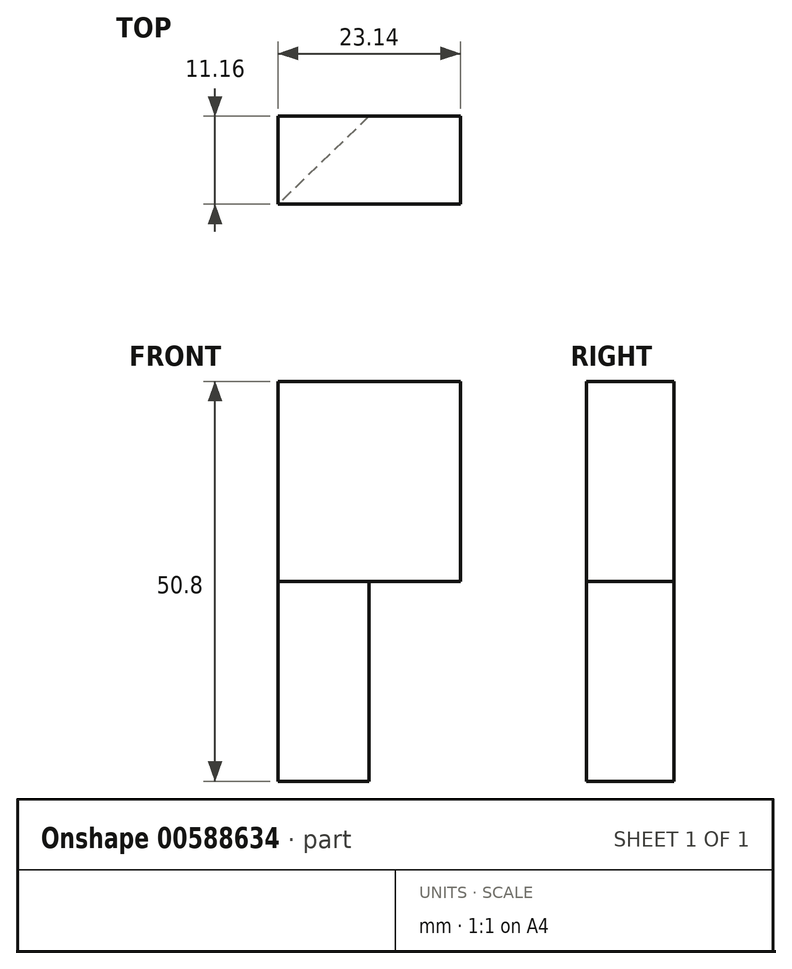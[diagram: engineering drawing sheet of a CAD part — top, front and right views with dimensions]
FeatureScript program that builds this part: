
annotation { "Feature Type Name" : "Feature", "Feature Type Description" : "" }
export const myFeature = defineFeature(function(context is Context, id is Id, definition is map)
    precondition{}
    {
        {
            var Q0;
            Q0=qCreatedBy(makeId("Top.planeOp"),FACE);
            var sketch = newSketch(context, id + "F0", { "sketchPlane" : qUnion([Q0])});
            skLineSegment(sketch, "E0.bottom", {"start": v(-11.57, -5.58) * mm, "end": v(11.57, -5.58) * mm});
            skLineSegment(sketch, "E0.top", {"start": v(-11.57, 5.58) * mm, "end": v(11.57, 5.58) * mm});
            skLineSegment(sketch, "E0.left", {"start": v(-11.57, -5.58) * mm, "end": v(-11.57, 5.58) * mm});
            skLineSegment(sketch, "E0.right", {"start": v(11.57, -5.58) * mm, "end": v(11.57, 5.58) * mm});
            skPoint(sketch, "E0.middle", {"position": v(0, 0) * mm});
            skSolve(sketch);
        }
        {
            var Q0;
            Q0=makeQuery(id+"F0.imprint","IMPRINT",FACE,{"disambiguationData":[TD([[makeQuery(id+"F0.imprint","IMPRINT",EDGE,{"derivedFrom":sQuery(id+"F0.wireOp",EDGE,"E0.bottom")}),1.0]])]});
            extrude(context, id + "F1", {"entities" : qUnion([Q0]), "depth" : 25.4 * mm, "offsetDistance" : 25.4 * mm});
        }
        {
            var Q0;
            Q0=makeQuery(id+"F1.opExtrude","CAP_FACE",FACE,{"disambiguationData":[OSD([sQuery(id+"F0.wireOp",EDGE,"E0.bottom"),sQuery(id+"F0.wireOp",EDGE,"E0.top"),sQuery(id+"F0.wireOp",EDGE,"E0.left"),sQuery(id+"F0.wireOp",EDGE,"E0.right")])],"isStart":false});
            var sketch = newSketch(context, id + "F2", { "sketchPlane" : qUnion([Q0])});
            skLineSegment(sketch, "E1", {"start": v(0, 5.58) * mm, "end": v(-11.57, -5.58) * mm});
            skSolve(sketch);
        }
        {
            var Q0;
            {var subQ0=sQuery(id+"F2.wireOp",EDGE,"E1");Q0=makeQuery(id+"F2.imprint","IMPRINT",FACE,{"disambiguationData":[TD([[makeQuery(id+"F2.imprint","IMPRINT",EDGE,{"derivedFrom":subQ0}),-1.0]])]});}
            extrude(context, id + "F3", {"entities" : qUnion([Q0]), "operationType" : NewBodyOperationType.ADD, "oppositeDirection" : true, "depth" : 50.8 * mm, "offsetDistance" : 25.4 * mm});
        }
    });
